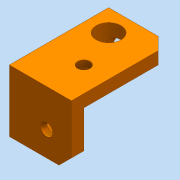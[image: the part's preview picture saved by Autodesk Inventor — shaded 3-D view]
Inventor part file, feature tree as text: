
AUTODESK INVENTOR PART (.ipt)
format: ipt  version: 2016 (Build 200138000, 138)  size: 185,856 bytes
history: native  units: mm
features: extrude x5, sketch x5, hole x4, chamfer x3, thicken_offset x1
ambient origin geometry x8: Origin, YZ Plane, XZ Plane, XY Plane, X Axis, Y Axis, Z Axis, Center Point
bodies: Solid1 (feature_tree)
feature tree (18):
  extrude  "Extrusion1"  Depth=20.0mm
  extrude  "Extrusion2"  Depth=16.0mm TaperAngle=0.0deg
  hole  "Hole2"  [1 undecoded]
  hole  "Hole3"  [1 undecoded]
  hole  "Hole4"  [1 undecoded]
  chamfer  "Chamfer1"  Distance=7.0mm
  chamfer  "Chamfer3"  Distance=7.0mm
  sketch  "Sketch3"  dims[d15=8.0mm d16=8.0mm d17=4.0mm d18=6.0mm d19=8.0mm d20=2.0mm d21=90.0deg d22=8.0mm d23=20.594885mm]
  sketch  "Sketch4"  dims[d24=8.0mm d25=8.0mm d26=4.0mm d27=6.0mm d28=8.0mm d29=2.0mm d30=90.0deg d31=8.0mm d32=20.594885mm]
  sketch  "Sketch5"  dims[d33=8.0mm d34=8.0mm d35=4.0mm d36=6.0mm d37=8.0mm d38=2.0mm d39=90.0deg d40=8.0mm d41=20.594885mm d42=4.0mm d43=2.0mm d44=45.0deg d48=4.0mm d49=2.0mm d50=45.0deg d51=7.0mm d52=7.0mm d53=7.0mm d54=2.0mm d55=0.0mm d56=2.0mm d57=0.0mm d58=2.0mm d59=0.0mm d60=7.0mm d61=25.0mm d62=8.0mm d63=6.0mm d64=4.0mm d65=2.0mm d66=90.0deg d67=8.0mm d68=20.594885mm d74=12.0mm d75=12.0mm d76=4.0mm d77=2.0mm d78=45.0deg]
  extrude  "Extrusion3"  Depth=2.0mm TaperAngle=0.0deg
  extrude  "Extrusion4"  Depth=2.0mm TaperAngle=0.0deg
  extrude  "Extrusion5"  Depth=2.0mm TaperAngle=0.0deg
  thicken_offset  "Thicken2"
  hole  "Hole5"  [1 undecoded]
  chamfer  "Chamfer4"  Distance=12.0mm
  sketch  "Sketch1"  dims[d0=20.0mm d1=20.0mm]
  sketch  "Sketch2"  dims[d2=4.0mm d3=0.0mm d4=16.0mm d5=0.0mm]
note: 4 required parameter values undecoded (feature->parameter linkage not recoverable at this tier; creation-order binding heuristic only, values carry confidence <= 0.55)
